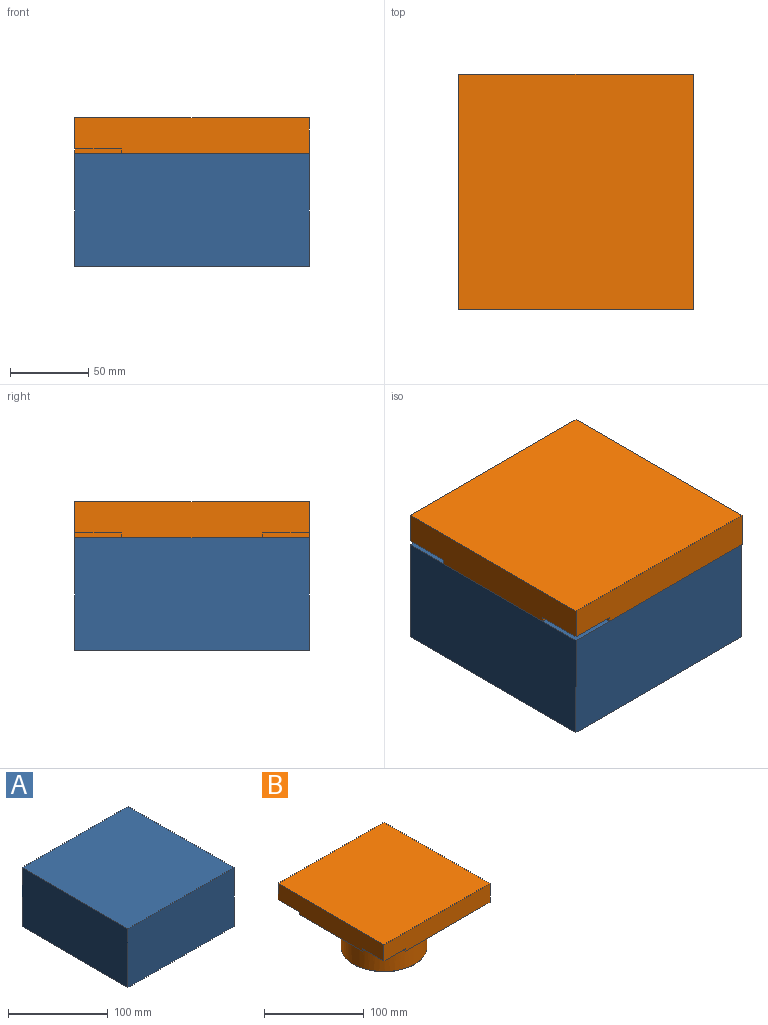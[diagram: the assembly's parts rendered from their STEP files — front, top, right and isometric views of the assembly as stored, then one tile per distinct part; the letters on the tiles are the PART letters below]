
ASSEMBLY  parts=2 mates=1
PART A: 12 faces, bbox 150x150x72 mm
  f0: plane 150x72mm, normal (1,0,0), area 10800mm2, adj f1,f3,f4,f6
  f1: plane 150x72mm, normal (0,1,0), area 10800mm2, adj f0,f2,f4,f6
  f2: plane 150x72mm, normal (-1,0,0), area 10800mm2, adj f1,f3,f4,f6
  f3: plane 150x72mm, normal (0,-1,0), area 10800mm2, adj f0,f2,f4,f6
  f4: plane 150x150mm, normal (0,0,1), area 22500mm2, adj f0,f1,f2,f3
  f5: cylinder r=60mm len=120mm, axis (0,0,1), area 754mm2, adj f6,f7
  f6: plane 150x150mm, normal (0,0,-1), area 11190.3mm2, adj f0,f1,f2,f3,f5
  f7: plane 120x120mm, normal (0,0,-1), area 4805.9mm2, adj f5,f10
  f8: cylinder r=45mm len=90mm, axis (0,0,-1), area 15268.1mm2, adj f10,f11
  f9: plane 89x89mm, normal (0,0,-1), area 6221.1mm2, adj f11
  f10: torus R=45.5mm, axis (0,0,1), area 223mm2, adj f7,f8
  f11: torus R=44.5mm, axis (0,0,1), area 221.2mm2, adj f8,f9
PART B: 16 faces, bbox 150x150x78 mm
  f0: plane 30x30mm, normal (0,0,-1), area 900mm2, adj f1,f2,f9,f10
  f1: plane 150x23mm, normal (0,1,0), area 3360mm2, adj f0,f2,f4,f5,f10,f11
  f2: plane 150x23mm, normal (-1,0,0), area 3270mm2, adj f0,f1,f3,f5,f6,f8,f9,f11
  f3: plane 150x23mm, normal (0,-1,0), area 3360mm2, adj f2,f4,f5,f6,f7,f11
  f4: plane 150x23mm, normal (1,0,0), area 3450mm2, adj f1,f3,f5,f11
  f5: plane 150x150mm, normal (0,0,1), area 22500mm2, adj f1,f2,f3,f4
  f6: plane 30x30mm, normal (0,0,-1), area 900mm2, adj f2,f3,f7,f8
  f7: plane 30x3mm, normal (-1,0,0), area 90mm2, adj f3,f6,f8,f11
  f8: plane 30x3mm, normal (0,-1,0), area 90mm2, adj f2,f6,f7,f11
  f9: plane 30x3mm, normal (0,1,0), area 90mm2, adj f0,f2,f10,f11
  f10: plane 30x3mm, normal (-1,0,0), area 90mm2, adj f0,f1,f9,f11
  f11: plane 150x150mm, normal (0,0,-1), area 14755.3mm2, adj f1,f2,f3,f4,f7,f8,f9,f10
  f12: plane 85x85mm, normal (0,0,-1), area 5674.5mm2, adj f14
  f13: cylinder r=43mm len=86mm, axis (0,0,1), area 14589.6mm2, adj f14,f15
  f14: torus R=42.5mm, axis (0,0,1), area 211.3mm2, adj f12,f13
  f15: torus R=43.5mm, axis (0,0,-1), area 213.1mm2, adj f11,f13
PLACE A rot(axis=(-1,0,0),180deg) t=(27.95,1.3,-82.88)mm
PLACE B t=(27.95,1.3,-77.88)mm
MATE fastened B.f2 <-> A.f2  axis (-1,0,0) through (-47.05,1.3,-80.88)mm
